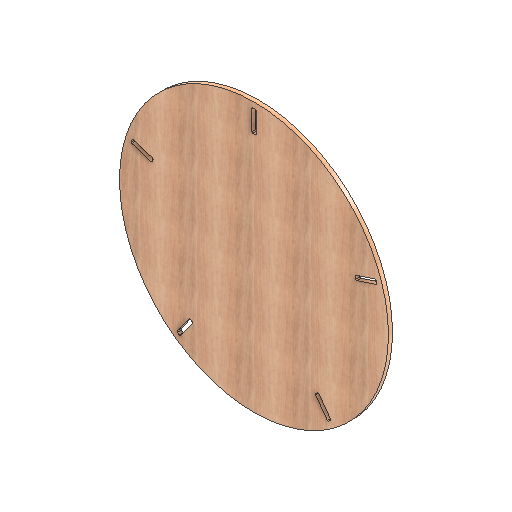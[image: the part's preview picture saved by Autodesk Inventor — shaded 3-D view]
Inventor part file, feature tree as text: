
AUTODESK INVENTOR PART (.ipt)
format: ipt  version: 2021 (Build 250183000, 183)  size: 360,448 bytes
history: native  units: mm
features: other x2, extrude x2, hole x1
ambient origin geometry x8: Origin, YZ Plane, XZ Plane, XY Plane, X Axis, Y Axis, Z Axis, Center Point
bodies: Body1 (feature_tree)
feature tree (5):
  other  "CONTOURS"
  hole  "HOLES"  [1 undecoded]
  other  "LETTERS"
  extrude  "Extrusion4"  Depth=1199.994596mm
  extrude  "Extrusion5"  Depth=90.0mm
note: 1 required parameter value undecoded (feature->parameter linkage not recoverable at this tier; creation-order binding heuristic only, values carry confidence <= 0.55)
